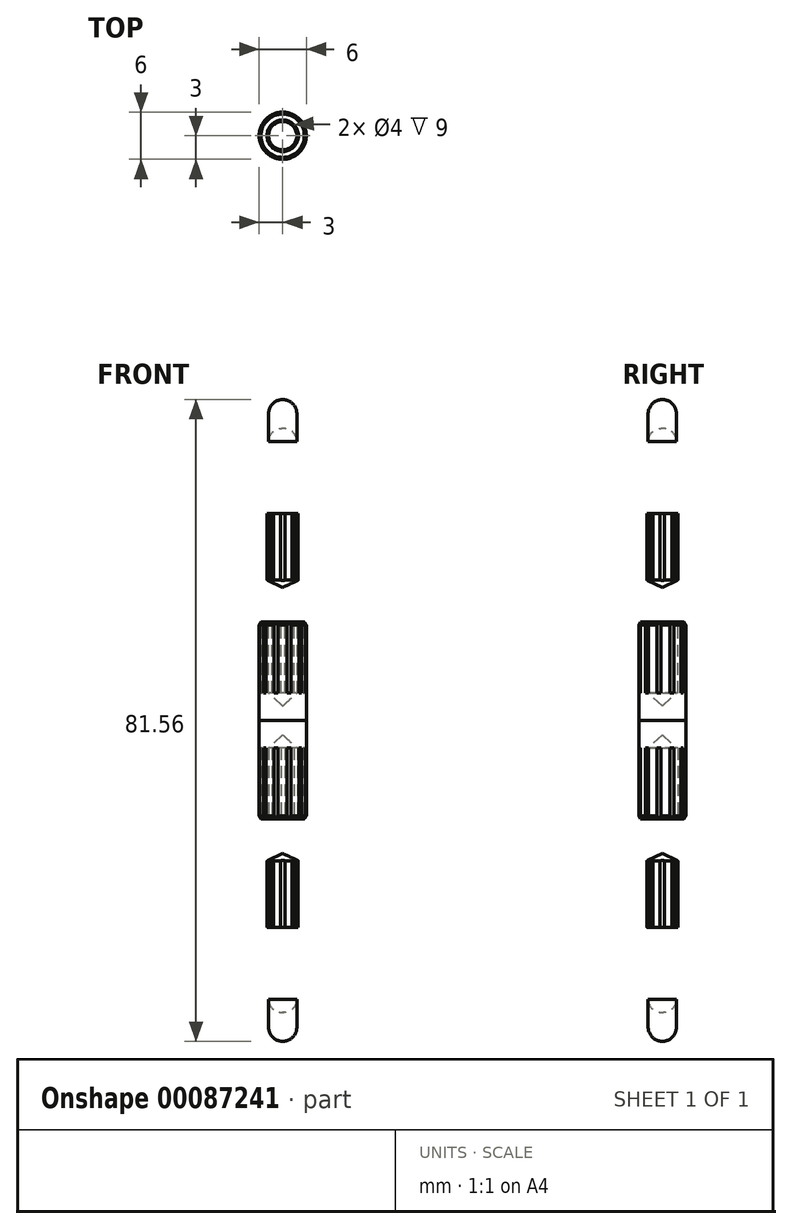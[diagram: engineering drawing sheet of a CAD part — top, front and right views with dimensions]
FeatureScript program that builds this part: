
annotation { "Feature Type Name" : "Feature", "Feature Type Description" : "" }
export const myFeature = defineFeature(function(context is Context, id is Id, definition is map)
    precondition{}
    {
        {
            var Q0;
            Q0=qCreatedBy(makeId("Front.planeOp"),FACE);
            var sketch = newSketch(context, id + "F0", { "sketchPlane" : qUnion([Q0]), "disableImprinting" : false});
            skLineSegment(sketch, "E0", {"start": v(0, 0) * mm, "end": v(3, 0) * mm});
            skLineSegment(sketch, "E1", {"start": v(3, 0) * mm, "end": v(3, 12.11) * mm});
            skLineSegment(sketch, "E2", {"start": v(2.75, 12.5) * mm, "end": v(2, 12.5) * mm});
            skLineSegment(sketch, "E3", {"start": v(2, 12.5) * mm, "end": v(2, 3.5) * mm});
            skLineSegment(sketch, "E4", {"start": v(2, 3.5) * mm, "end": v(1.81, 3.5) * mm});
            skLineSegment(sketch, "E5", {"start": v(0, 1.84) * mm, "end": v(0, 0) * mm});
            skLineSegment(sketch, "E6", {"start": v(2.75, 12.5) * mm, "end": v(3, 12.11) * mm});
            skLineSegment(sketch, "E7", {"start": v(1.81, 3.5) * mm, "end": v(0, 1.84) * mm});
            skPoint(sketch, "E8.orphan", {"position": v(0, 3.5) * mm});
            skSolve(sketch);
        }
        {
            var Q0;
            Q0=makeQuery(id+"F0.imprint","IMPRINT",FACE,{"disambiguationData":[TD([[makeQuery(id+"F0.imprint","IMPRINT",EDGE,{"derivedFrom":sQuery(id+"F0.wireOp",EDGE,"E0")}),1.0]])]});
            var Q1;
            Q1=sQuery(id+"F0.wireOp",EDGE,"E5");
            revolve(context, id + "F1", {"entities" : qUnion([Q0]), "axis" : qUnion([Q1]), "revolveType" : RevolveType.FULL});
        }
        {
            var Q0;
            Q0=qCreatedBy(makeId("Front.planeOp"),FACE);
            var sketch = newSketch(context, id + "F2", { "sketchPlane" : qUnion([Q0]), "disableImprinting" : false});
            skLineSegment(sketch, "E9", {"start": v(0, 16.9) * mm, "end": v(0, 26.27) * mm});
            skLineSegment(sketch, "E10", {"start": v(1.99, 26.27) * mm, "end": v(1.99, 17.83) * mm});
            skLineSegment(sketch, "E11", {"start": v(1.99, 17.83) * mm, "end": v(0, 16.9) * mm});
            skLineSegment(sketch, "E12", {"start": v(0, 26.27) * mm, "end": v(1.99, 26.27) * mm});
            skSolve(sketch);
        }
        {
            var Q0;
            Q0=qCreatedBy(makeId("Front.planeOp"),FACE);
            var sketch = newSketch(context, id + "F3", { "sketchPlane" : qUnion([Q0]), "disableImprinting" : false});
            skLineSegment(sketch, "E13", {"start": v(0, 40.78) * mm, "end": v(0, 33.78) * mm});
            skLineSegment(sketch, "E14", {"start": v(1.8, 38.93) * mm, "end": v(1.8, 35.43) * mm});
            skArc(sketch, "E15", {"start": v(1.8, 38.93) * mm, "mid": v(1.28, 40.22) * mm, "end": v(0, 40.78) * mm});
            skArc(sketch, "E16", {"start": v(0, 33.78) * mm, "mid": v(1.26, 34.2) * mm, "end": v(1.8, 35.43) * mm});
            skSolve(sketch);
        }
        {
            var Q0;
            Q0=makeQuery(id+"F3.imprint","IMPRINT",FACE,{"disambiguationData":[TD([[makeQuery(id+"F3.imprint","IMPRINT",EDGE,{"derivedFrom":sQuery(id+"F3.wireOp",EDGE,"E13")}),1.0]])]});
            var Q1;
            Q1=sQuery(id+"F3.wireOp",EDGE,"E13");
            revolve(context, id + "F4", {"entities" : qUnion([Q0]), "axis" : qUnion([Q1]), "revolveType" : RevolveType.FULL});
        }
        {
            var Q0;
            Q0=makeQuery(id+"F2.imprint","IMPRINT",FACE,{"disambiguationData":[TD([[makeQuery(id+"F2.imprint","IMPRINT",EDGE,{"derivedFrom":sQuery(id+"F2.wireOp",EDGE,"E9")}),-1.0]])]});
            var Q1;
            Q1=sQuery(id+"F2.wireOp",EDGE,"E9");
            revolve(context, id + "F5", {"entities" : qUnion([Q0]), "axis" : qUnion([Q1]), "revolveType" : RevolveType.FULL});
        }
        {
            var Q0;
            Q0=makeQuery(id+"F5.opRevolve","SWEPT_FACE",FACE,{"disambiguationData":[OSD([sQuery(id+"F2.wireOp",EDGE,"E12")])]});
            var sketch = newSketch(context, id + "F6", { "sketchPlane" : qUnion([Q0])});
            skArc(sketch, "E17", {"start": v(-0.42, 2.08) * mm, "mid": v(-0.83, 1.96) * mm, "end": v(-1.2, 1.75) * mm});
            skArc(sketch, "E18", {"start": v(-0.42, 2.08) * mm, "mid": v(-0.01, 1.88) * mm, "end": v(0.4, 2.09) * mm});
            skArc(sketch, "E19.1.0", {"start": v(-1.77, 1.17) * mm, "mid": v(-1.34, 1.32) * mm, "end": v(-1.2, 1.75) * mm});
            skArc(sketch, "E19.2.0", {"start": v(-2.08, -0.42) * mm, "mid": v(-1.88, -0.01) * mm, "end": v(-2.09, 0.4) * mm});
            skArc(sketch, "E19.3.0", {"start": v(-1.17, -1.77) * mm, "mid": v(-1.32, -1.34) * mm, "end": v(-1.75, -1.2) * mm});
            skArc(sketch, "E19.4.0", {"start": v(0.42, -2.08) * mm, "mid": v(0.01, -1.88) * mm, "end": v(-0.4, -2.09) * mm});
            skArc(sketch, "E19.5.0", {"start": v(1.77, -1.17) * mm, "mid": v(1.34, -1.32) * mm, "end": v(1.2, -1.75) * mm});
            skArc(sketch, "E19.6.0", {"start": v(2.08, 0.42) * mm, "mid": v(1.88, 0.01) * mm, "end": v(2.09, -0.4) * mm});
            skArc(sketch, "E19.7.0", {"start": v(1.17, 1.77) * mm, "mid": v(1.32, 1.34) * mm, "end": v(1.75, 1.2) * mm});
            skArc(sketch, "E20.trimOffspring", {"start": v(1.17, 1.77) * mm, "mid": v(0.8, 1.97) * mm, "end": v(0.4, 2.09) * mm});
            skArc(sketch, "E21.trimOffspring", {"start": v(2.08, 0.42) * mm, "mid": v(1.96, 0.83) * mm, "end": v(1.75, 1.2) * mm});
            skArc(sketch, "E22.trimOffspring", {"start": v(1.77, -1.17) * mm, "mid": v(1.97, -0.8) * mm, "end": v(2.09, -0.4) * mm});
            skArc(sketch, "E23.trimOffspring", {"start": v(-1.77, 1.17) * mm, "mid": v(-1.97, 0.8) * mm, "end": v(-2.09, 0.4) * mm});
            skArc(sketch, "E24.trimOffspring", {"start": v(-2.08, -0.42) * mm, "mid": v(-1.96, -0.83) * mm, "end": v(-1.75, -1.2) * mm});
            skArc(sketch, "E25.trimOffspring", {"start": v(-1.17, -1.77) * mm, "mid": v(-0.8, -1.97) * mm, "end": v(-0.4, -2.09) * mm});
            skArc(sketch, "E26.trimOffspring", {"start": v(0.42, -2.08) * mm, "mid": v(0.83, -1.96) * mm, "end": v(1.2, -1.75) * mm});
            skCircle(sketch, "E27", {"center": v(0, 0) * mm, "radius": 2.36 * mm});
            skSolve(sketch);
        }
        {
            var Q0;
            Q0 = qSketchRegion(id + "F6", true);
            extrude(context, id + "F7", {"entities" : qUnion([Q0]), "operationType" : NewBodyOperationType.REMOVE, "oppositeDirection" : true, "depth" : 9 * mm});
        }
        {
            var Q0;
            Q0=makeQuery(id+"F1.opRevolve","SWEPT_FACE",FACE,{"disambiguationData":[OSD([sQuery(id+"F0.wireOp",EDGE,"E2")])]});
            var sketch = newSketch(context, id + "F8", { "sketchPlane" : qUnion([Q0])});
            skCircle(sketch, "E28", {"center": v(0, 0) * mm, "radius": 3.35 * mm});
            skArc(sketch, "E29", {"start": v(-0.29, 3.07) * mm, "mid": v(-0.84, 2.96) * mm, "end": v(-1.36, 2.76) * mm});
            skArc(sketch, "E30", {"start": v(-0.29, 3.07) * mm, "mid": v(0.03, 2.88) * mm, "end": v(0.34, 3.06) * mm});
            skArc(sketch, "E31.1.0", {"start": v(-1.9, 2.42) * mm, "mid": v(-1.53, 2.43) * mm, "end": v(-1.36, 2.76) * mm});
            skArc(sketch, "E31.2.0", {"start": v(-2.9, 1.01) * mm, "mid": v(-2.6, 1.22) * mm, "end": v(-2.64, 1.58) * mm});
            skArc(sketch, "E31.3.0", {"start": v(-3, -0.72) * mm, "mid": v(-2.85, -0.38) * mm, "end": v(-3.08, -0.1) * mm});
            skArc(sketch, "E31.4.0", {"start": v(-2.13, -2.23) * mm, "mid": v(-2.2, -1.86) * mm, "end": v(-2.54, -1.74) * mm});
            skArc(sketch, "E31.5.0", {"start": v(-0.59, -3.02) * mm, "mid": v(-0.84, -2.75) * mm, "end": v(-1.2, -2.84) * mm});
            skArc(sketch, "E31.6.0", {"start": v(1.14, -2.86) * mm, "mid": v(0.79, -2.77) * mm, "end": v(0.53, -3.03) * mm});
            skArc(sketch, "E31.7.0", {"start": v(2.5, -1.79) * mm, "mid": v(2.16, -1.9) * mm, "end": v(2.09, -2.26) * mm});
            skArc(sketch, "E31.8.0", {"start": v(3.08, -0.15) * mm, "mid": v(2.84, -0.44) * mm, "end": v(2.98, -0.78) * mm});
            skArc(sketch, "E31.9.0", {"start": v(2.67, 1.54) * mm, "mid": v(2.63, 1.17) * mm, "end": v(2.93, 0.96) * mm});
            skArc(sketch, "E31.10.0", {"start": v(1.41, 2.74) * mm, "mid": v(1.58, 2.4) * mm, "end": v(1.94, 2.39) * mm});
            skArc(sketch, "E32.trimOffspring", {"start": v(1.41, 2.74) * mm, "mid": v(0.9, 2.95) * mm, "end": v(0.34, 3.06) * mm});
            skArc(sketch, "E33.trimOffspring", {"start": v(-1.9, 2.42) * mm, "mid": v(-2.3, 2.04) * mm, "end": v(-2.64, 1.58) * mm});
            skArc(sketch, "E34.trimOffspring", {"start": v(2.67, 1.54) * mm, "mid": v(2.35, 2) * mm, "end": v(1.94, 2.39) * mm});
            skArc(sketch, "E35.trimOffspring", {"start": v(-2.9, 1.01) * mm, "mid": v(-3.04, 0.47) * mm, "end": v(-3.08, -0.1) * mm});
            skArc(sketch, "E36.trimOffspring", {"start": v(3.08, -0.15) * mm, "mid": v(3.05, 0.41) * mm, "end": v(2.93, 0.96) * mm});
            skArc(sketch, "E37.trimOffspring", {"start": v(2.5, -1.79) * mm, "mid": v(2.8, -1.3) * mm, "end": v(2.98, -0.78) * mm});
            skArc(sketch, "E38.trimOffspring", {"start": v(1.14, -2.86) * mm, "mid": v(1.64, -2.6) * mm, "end": v(2.09, -2.26) * mm});
            skArc(sketch, "E39.trimOffspring", {"start": v(-0.59, -3.02) * mm, "mid": v(-0.03, -3.08) * mm, "end": v(0.53, -3.03) * mm});
            skArc(sketch, "E40.trimOffspring", {"start": v(-2.13, -2.23) * mm, "mid": v(-1.69, -2.58) * mm, "end": v(-1.2, -2.84) * mm});
            skArc(sketch, "E41.trimOffspring", {"start": v(-3, -0.72) * mm, "mid": v(-2.81, -1.25) * mm, "end": v(-2.54, -1.74) * mm});
            skSolve(sketch);
        }
        {
            var Q0;
            Q0 = qSketchRegion(id + "F8", true);
            extrude(context, id + "F9", {"entities" : qUnion([Q0]), "operationType" : NewBodyOperationType.REMOVE, "oppositeDirection" : true, "depth" : 9 * mm});
        }
        {
            var Q0;
            Q0=makeQuery(id+"F1.opRevolve","SWEPT_BODY",BODY,{"disambiguationData":[OSD([sQuery(id+"F0.wireOp",EDGE,"E0"),sQuery(id+"F0.wireOp",EDGE,"E1"),sQuery(id+"F0.wireOp",EDGE,"E2"),sQuery(id+"F0.wireOp",EDGE,"E3"),sQuery(id+"F0.wireOp",EDGE,"E4"),sQuery(id+"F0.wireOp",EDGE,"E5"),sQuery(id+"F0.wireOp",EDGE,"E6"),sQuery(id+"F0.wireOp",EDGE,"E7")])]});
            var Q1;
            Q1=qCreatedBy(makeId("Top.planeOp"),FACE);
            mirror(context, id + "F10", {"operationType" : NewBodyOperationType.ADD, "entities" : qUnion([Q0]), "mirrorPlane" : qUnion([Q1])});
        }
        {
            var Q0;
            Q0=makeQuery(id+"F5.opRevolve","SWEPT_BODY",BODY,{"disambiguationData":[OSD([sQuery(id+"F2.wireOp",EDGE,"E9"),sQuery(id+"F2.wireOp",EDGE,"E10"),sQuery(id+"F2.wireOp",EDGE,"E11"),sQuery(id+"F2.wireOp",EDGE,"E12")])]});
            var Q1;
            Q1=qCreatedBy(makeId("Top.planeOp"),FACE);
            mirror(context, id + "F11", {"entities" : qUnion([Q0]), "mirrorPlane" : qUnion([Q1])});
        }
        {
            var Q0;
            Q0=makeQuery(id+"F4.opRevolve","SWEPT_BODY",BODY,{"disambiguationData":[OSD([sQuery(id+"F3.wireOp",EDGE,"E13"),sQuery(id+"F3.wireOp",EDGE,"E14"),sQuery(id+"F3.wireOp",EDGE,"E15"),sQuery(id+"F3.wireOp",EDGE,"E16")])]});
            var Q1;
            Q1=qCreatedBy(makeId("Top.planeOp"),FACE);
            mirror(context, id + "F12", {"entities" : qUnion([Q0]), "mirrorPlane" : qUnion([Q1])});
        }
    });
